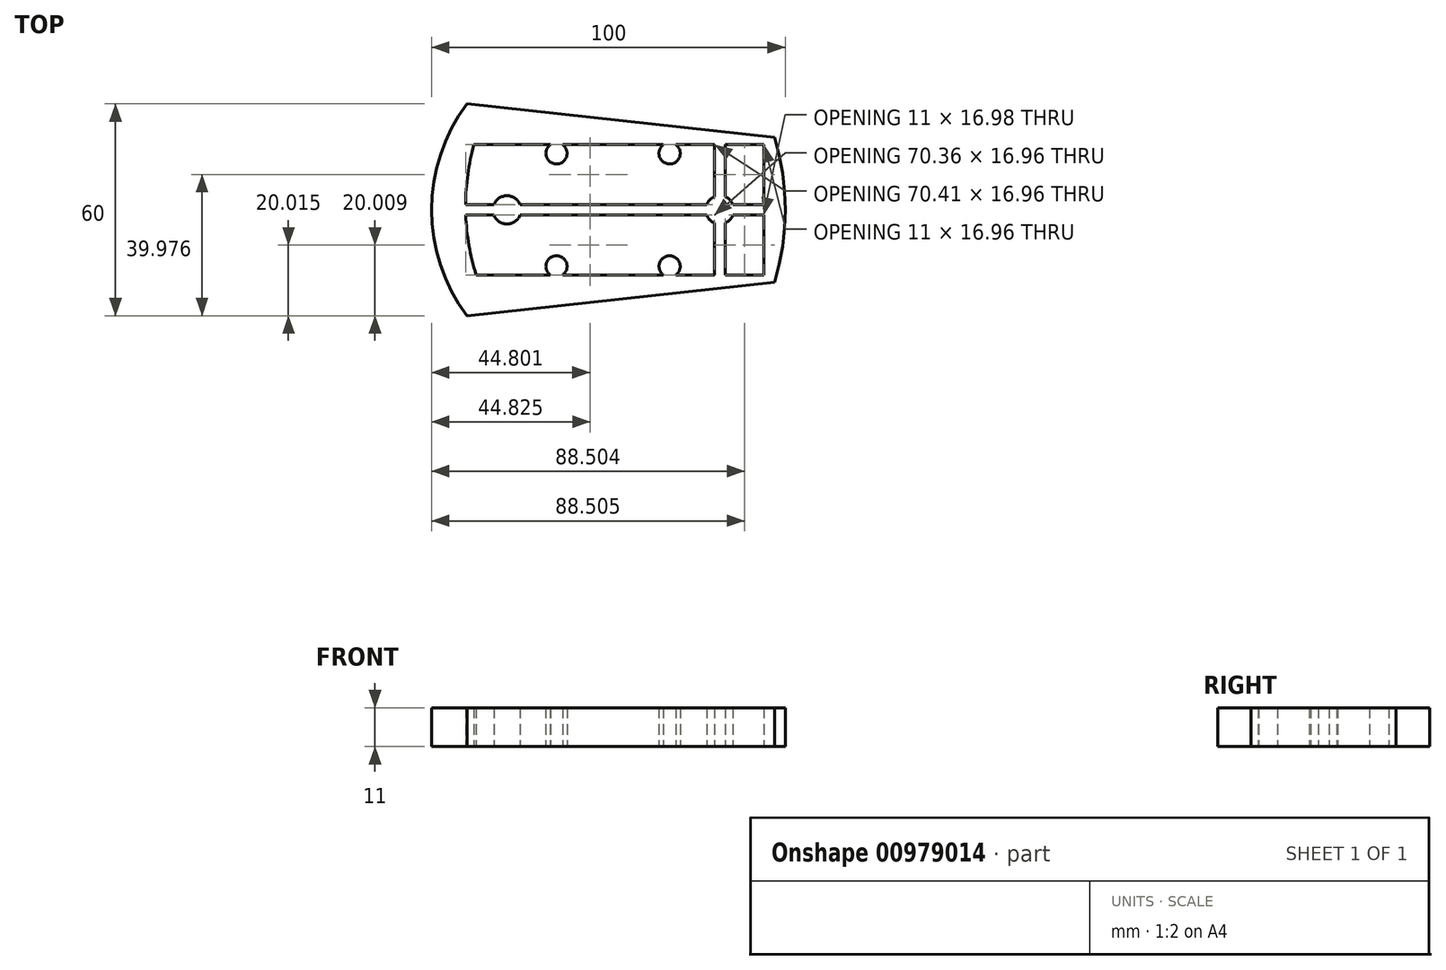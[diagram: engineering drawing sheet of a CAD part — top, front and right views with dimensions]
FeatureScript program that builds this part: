
annotation { "Feature Type Name" : "Feature", "Feature Type Description" : "" }
export const myFeature = defineFeature(function(context is Context, id is Id, definition is map)
    precondition{}
    {
        {
            var Q0;
            Q0=qCreatedBy(makeId("Top.planeOp"),FACE);
            var sketch = newSketch(context, id + "F0", { "sketchPlane" : qUnion([Q0])});
            skLineSegment(sketch, "E0.bottom", {"start": v(-45.83, -20.28) * mm, "end": v(42.17, -20.28) * mm});
            skLineSegment(sketch, "E0.top", {"start": v(-45.83, 20.72) * mm, "end": v(42.17, 20.72) * mm});
            skLineSegment(sketch, "E0.right", {"start": v(42.17, -20.28) * mm, "end": v(42.17, 20.72) * mm});
            skPoint(sketch, "E0.middle", {"position": v(-1.83, 0.22) * mm});
            skLineSegment(sketch, "E1", {"start": v(42.17, 20.72) * mm, "end": v(-44.83, 30.22) * mm});
            skLineSegment(sketch, "E2.MirrorCS", {"start": v(42.17, -20.28) * mm, "end": v(-44.83, -29.78) * mm});
            skArc(sketch, "E3", {"start": v(-44.83, 30.22) * mm, "mid": v(-54.83, 0.22) * mm, "end": v(-44.83, -29.78) * mm});
            skArc(sketch, "E4", {"start": v(42.17, -20.28) * mm, "mid": v(45.17, 0.22) * mm, "end": v(42.17, 20.72) * mm});
            skLineSegment(sketch, "E5.1", {"start": v(-42.25, -18.19) * mm, "end": v(39.17, -18.26) * mm});
            skLineSegment(sketch, "E5.2", {"start": v(39.17, -18.26) * mm, "end": v(39.17, 18.68) * mm});
            skLineSegment(sketch, "E5.3", {"start": v(-42.85, 18.68) * mm, "end": v(39.17, 18.68) * mm});
            skArc(sketch, "E6", {"start": v(-45.83, 20.72) * mm, "mid": v(-48.83, 0.22) * mm, "end": v(-45.83, -20.28) * mm});
            skArc(sketch, "E7", {"start": v(-42.85, 18.68) * mm, "mid": v(-45.23, 0.2) * mm, "end": v(-42.25, -18.19) * mm});
            skPoint(sketch, "E8", {"position": v(26.67, 0.22) * mm});
            skPoint(sketch, "E9", {"position": v(-33.53, 0.22) * mm});
            skPoint(sketch, "E10", {"position": v(-19.53, 16.22) * mm});
            skPoint(sketch, "E11", {"position": v(-19.53, -15.78) * mm});
            skPoint(sketch, "E12", {"position": v(44.47, 16.22) * mm});
            skCircle(sketch, "E13", {"center": v(-19.53, 16.22) * mm, "radius": 3 * mm});
            skCircle(sketch, "E14", {"center": v(-19.53, 16.22) * mm, "radius": 1.3 * mm});
            skCircle(sketch, "E15.MirrorC", {"center": v(12.47, 16.22) * mm, "radius": 1.3 * mm});
            skCircle(sketch, "E16.MirrorC", {"center": v(-19.53, -15.78) * mm, "radius": 3 * mm});
            skCircle(sketch, "E17.MirrorC", {"center": v(12.47, 16.22) * mm, "radius": 3 * mm});
            skCircle(sketch, "E18.MirrorC", {"center": v(-19.53, -15.78) * mm, "radius": 1.3 * mm});
            skPoint(sketch, "E19.MirrorP", {"position": v(12.47, -15.78) * mm});
            skCircle(sketch, "E20.1.0.0", {"center": v(12.47, -15.78) * mm, "radius": 3 * mm});
            skCircle(sketch, "E20.1.0.1", {"center": v(12.47, -15.78) * mm, "radius": 1.3 * mm});
            skLineSegment(sketch, "E20.direction1", {"start": v(-19.53, -15.78) * mm, "end": v(12.47, -15.78) * mm, "construction": true});
            skCircle(sketch, "E21", {"center": v(-33.53, 0.22) * mm, "radius": 4 * mm});
            skCircle(sketch, "E22", {"center": v(-33.53, 0.22) * mm, "radius": 1.3 * mm});
            skCircle(sketch, "E23.1.0.0", {"center": v(26.67, 0.22) * mm, "radius": 1.3 * mm});
            skArc(sketch, "E23.1.0.1", {"start": v(28.17, -3.5) * mm, "mid": v(30.67, 0.22) * mm, "end": v(28.17, 3.93) * mm});
            skLineSegment(sketch, "E23.direction1", {"start": v(-33.53, 0.22) * mm, "end": v(26.67, 0.22) * mm, "construction": true});
            skLineSegment(sketch, "E24", {"start": v(-45.23, 1.72) * mm, "end": v(39.17, 1.72) * mm});
            skLineSegment(sketch, "E25.direction1", {"start": v(-45.23, 1.72) * mm, "end": v(-45.23, 1.72) * mm});
            skLineSegment(sketch, "E26", {"start": v(-45.18, -1.28) * mm, "end": v(39.17, -1.28) * mm});
            skLineSegment(sketch, "E27", {"start": v(11.95, 13.25) * mm, "end": v(11.95, -12.83) * mm});
            skLineSegment(sketch, "E28", {"start": v(14.9, 14.42) * mm, "end": v(14.9, -14) * mm});
            skLineSegment(sketch, "E29", {"start": v(25.17, 3.93) * mm, "end": v(25.17, 18.68) * mm});
            skLineSegment(sketch, "E30", {"start": v(28.17, 3.93) * mm, "end": v(28.17, 18.68) * mm});
            skLineSegment(sketch, "E31", {"start": v(-21.37, -13.42) * mm, "end": v(-21.37, -1.28) * mm});
            skLineSegment(sketch, "E32", {"start": v(-21.37, 1.72) * mm, "end": v(-21.37, 13.85) * mm});
            skLineSegment(sketch, "E33", {"start": v(-4.83, -18.22) * mm, "end": v(-4.83, -1.28) * mm});
            skLineSegment(sketch, "E34", {"start": v(-4.83, -1.28) * mm, "end": v(-4.83, 1.72) * mm});
            skLineSegment(sketch, "E35", {"start": v(-4.83, 1.72) * mm, "end": v(-4.83, 18.68) * mm});
            skArc(sketch, "E36.trimOffspring", {"start": v(25.17, 3.93) * mm, "mid": v(22.67, 0.22) * mm, "end": v(25.17, -3.5) * mm});
            skArc(sketch, "E37", {"start": v(25.17, 3.93) * mm, "mid": v(30.67, 0.22) * mm, "end": v(25.17, -3.5) * mm});
            skLineSegment(sketch, "E38", {"start": v(25.17, -3.5) * mm, "end": v(25.17, -18.25) * mm});
            skLineSegment(sketch, "E39", {"start": v(28.17, -3.5) * mm, "end": v(28.17, -18.25) * mm});
            skSolve(sketch);
        }
        {
            var Q0;
            Q0=makeQuery(id+"F0.imprint","IMPRINT",FACE,{"disambiguationData":[TD([[makeQuery(id+"F0.imprint","IMPRINT",EDGE,{"derivedFrom":sQuery(id+"F0.wireOp",EDGE,"E0.bottom")}),-1.0]])]});
            var Q1;
            {var subQ0=sQuery(id+"F0.wireOp",EDGE,"E38");Q1=makeQuery(id+"F0.imprint","IMPRINT",FACE,{"disambiguationData":[TD([[makeQuery(id+"F0.imprint","IMPRINT",EDGE,{"derivedFrom":subQ0}),1.0]])]});}
            var Q2;
            {var subQ0=sQuery(id+"F0.wireOp",EDGE,"E26");var subQ1=sQuery(id+"F0.wireOp",EDGE,"E21");var subQ2=makeQuery(id+"F0.imprint","INTERSECT",VERTEX,{"disambiguationData":[OD(0.0)],"derivedFrom":[subQ1,subQ0]});Q2=makeQuery(id+"F0.imprint","IMPRINT",FACE,{"disambiguationData":[TD([[makeQuery(id+"F0.imprint","IMPRINT",EDGE,{"disambiguationData":[TD([[subQ2,-1.0]])],"derivedFrom":subQ1}),1.0]])]});}
            var Q3;
            Q3=makeQuery(id+"F0.imprint","IMPRINT",FACE,{"disambiguationData":[TD([[makeQuery(id+"F0.imprint","IMPRINT",EDGE,{"derivedFrom":sQuery(id+"F0.wireOp",EDGE,"E18.MirrorC")}),1.0]])]});
            var Q4;
            Q4=makeQuery(id+"F0.imprint","IMPRINT",FACE,{"disambiguationData":[TD([[makeQuery(id+"F0.imprint","IMPRINT",EDGE,{"derivedFrom":sQuery(id+"F0.wireOp",EDGE,"E0.right")}),-1.0]])]});
            var Q5;
            Q5=makeQuery(id+"F0.imprint","IMPRINT",FACE,{"disambiguationData":[TD([[makeQuery(id+"F0.imprint","IMPRINT",EDGE,{"derivedFrom":sQuery(id+"F0.wireOp",EDGE,"E15.MirrorC")}),-1.0]])]});
            var Q6;
            {var subQ0=sQuery(id+"F0.wireOp",EDGE,"E24");var subQ1=sQuery(id+"F0.wireOp",EDGE,"E21");var subQ2=makeQuery(id+"F0.imprint","INTERSECT",VERTEX,{"disambiguationData":[OD(0.0)],"derivedFrom":[subQ1,subQ0]});Q6=makeQuery(id+"F0.imprint","IMPRINT",FACE,{"disambiguationData":[TD([[makeQuery(id+"F0.imprint","IMPRINT",EDGE,{"disambiguationData":[TD([[subQ2,1.0]])],"derivedFrom":subQ1}),1.0]])]});}
            var Q7;
            Q7=makeQuery(id+"F0.imprint","IMPRINT",FACE,{"disambiguationData":[TD([[makeQuery(id+"F0.imprint","IMPRINT",EDGE,{"derivedFrom":sQuery(id+"F0.wireOp",EDGE,"E20.1.0.1")}),1.0]])]});
            var Q8;
            {var subQ0=sQuery(id+"F0.wireOp",EDGE,"E24");var subQ1=sQuery(id+"F0.wireOp",EDGE,"E5.2");var subQ2=makeQuery(id+"F0.imprint","INTERSECT",VERTEX,{"derivedFrom":[subQ1,subQ0]});Q8=makeQuery(id+"F0.imprint","IMPRINT",FACE,{"disambiguationData":[TD([[makeQuery(id+"F0.imprint","IMPRINT",EDGE,{"disambiguationData":[TD([[subQ2,1.0]])],"derivedFrom":subQ1}),1.0]])]});}
            var Q9;
            Q9=makeQuery(id+"F0.imprint","IMPRINT",FACE,{"disambiguationData":[TD([[makeQuery(id+"F0.imprint","IMPRINT",EDGE,{"derivedFrom":sQuery(id+"F0.wireOp",EDGE,"E15.MirrorC")}),1.0]])]});
            var Q10;
            Q10=makeQuery(id+"F0.imprint","IMPRINT",FACE,{"disambiguationData":[TD([[makeQuery(id+"F0.imprint","IMPRINT",EDGE,{"derivedFrom":sQuery(id+"F0.wireOp",EDGE,"E14")}),-1.0]])]});
            var Q11;
            Q11=makeQuery(id+"F0.imprint","IMPRINT",FACE,{"disambiguationData":[TD([[makeQuery(id+"F0.imprint","IMPRINT",EDGE,{"derivedFrom":sQuery(id+"F0.wireOp",EDGE,"E22")}),-1.0]])]});
            var Q12;
            {var subQ0=sQuery(id+"F0.wireOp",EDGE,"E29");Q12=makeQuery(id+"F0.imprint","IMPRINT",FACE,{"disambiguationData":[TD([[makeQuery(id+"F0.imprint","IMPRINT",EDGE,{"derivedFrom":subQ0}),-1.0]])]});}
            var Q13;
            Q13=makeQuery(id+"F0.imprint","IMPRINT",FACE,{"disambiguationData":[TD([[makeQuery(id+"F0.imprint","IMPRINT",EDGE,{"derivedFrom":sQuery(id+"F0.wireOp",EDGE,"E23.1.0.0")}),-1.0]])]});
            var Q14;
            {var subQ0=sQuery(id+"F0.wireOp",EDGE,"E24");var subQ1=sQuery(id+"F0.wireOp",EDGE,"E7");var subQ2=makeQuery(id+"F0.imprint","INTERSECT",VERTEX,{"derivedFrom":[subQ1,subQ0]});Q14=makeQuery(id+"F0.imprint","IMPRINT",FACE,{"disambiguationData":[TD([[makeQuery(id+"F0.imprint","IMPRINT",EDGE,{"disambiguationData":[TD([[subQ2,-1.0]])],"derivedFrom":subQ1}),1.0]])]});}
            var Q15;
            {var subQ0=sQuery(id+"F0.wireOp",EDGE,"E27");var subQ1=sQuery(id+"F0.wireOp",EDGE,"E17.MirrorC");var subQ2=makeQuery(id+"F0.imprint","INTERSECT",VERTEX,{"derivedFrom":[subQ1,subQ0]});Q15=makeQuery(id+"F0.imprint","IMPRINT",FACE,{"disambiguationData":[TD([[makeQuery(id+"F0.imprint","IMPRINT",EDGE,{"disambiguationData":[TD([[subQ2,1.0]])],"derivedFrom":subQ1}),1.0]])]});}
            var Q16;
            {var subQ0=sQuery(id+"F0.wireOp",EDGE,"E27");var subQ1=sQuery(id+"F0.wireOp",EDGE,"E20.1.0.0");var subQ2=makeQuery(id+"F0.imprint","INTERSECT",VERTEX,{"derivedFrom":[subQ1,subQ0]});Q16=makeQuery(id+"F0.imprint","IMPRINT",FACE,{"disambiguationData":[TD([[makeQuery(id+"F0.imprint","IMPRINT",EDGE,{"disambiguationData":[TD([[subQ2,-1.0]])],"derivedFrom":subQ1}),1.0]])]});}
            var Q17;
            {var subQ0=sQuery(id+"F0.wireOp",EDGE,"E34");Q17=makeQuery(id+"F0.imprint","IMPRINT",FACE,{"disambiguationData":[TD([[makeQuery(id+"F0.imprint","IMPRINT",EDGE,{"derivedFrom":subQ0}),-1.0]])]});}
            var Q18;
            {var subQ0=sQuery(id+"F0.wireOp",EDGE,"E27");var subQ1=sQuery(id+"F0.wireOp",EDGE,"E24");var subQ2=makeQuery(id+"F0.imprint","INTERSECT",VERTEX,{"derivedFrom":[subQ1,subQ0]});Q18=makeQuery(id+"F0.imprint","IMPRINT",FACE,{"disambiguationData":[TD([[makeQuery(id+"F0.imprint","IMPRINT",EDGE,{"disambiguationData":[TD([[subQ2,-1.0]])],"derivedFrom":subQ1}),-1.0]])]});}
            var Q19;
            {var subQ6=sQuery(id+"F0.wireOp",EDGE,"E34");Q19=makeQuery(id+"F0.imprint","IMPRINT",FACE,{"disambiguationData":[TD([[makeQuery(id+"F0.imprint","IMPRINT",EDGE,{"derivedFrom":subQ6}),1.0]])]});}
            var Q20;
            {var subQ0=sQuery(id+"F0.wireOp",EDGE,"E28");var subQ1=sQuery(id+"F0.wireOp",EDGE,"E24");var subQ2=makeQuery(id+"F0.imprint","INTERSECT",VERTEX,{"derivedFrom":[subQ1,subQ0]});Q20=makeQuery(id+"F0.imprint","IMPRINT",FACE,{"disambiguationData":[TD([[makeQuery(id+"F0.imprint","IMPRINT",EDGE,{"disambiguationData":[TD([[subQ2,-1.0]])],"derivedFrom":subQ1}),-1.0]])]});}
            var Q21;
            Q21=makeQuery(id+"F0.imprint","IMPRINT",FACE,{"disambiguationData":[TD([[makeQuery(id+"F0.imprint","IMPRINT",EDGE,{"derivedFrom":sQuery(id+"F0.wireOp",EDGE,"E0.bottom")}),1.0]])]});
            var Q22;
            {var subQ0=sQuery(id+"F0.wireOp",EDGE,"E36.trimOffspring");var subQ1=sQuery(id+"F0.wireOp",EDGE,"E24");var subQ2=makeQuery(id+"F0.imprint","INTERSECT",VERTEX,{"derivedFrom":[subQ1,subQ0]});Q22=makeQuery(id+"F0.imprint","IMPRINT",FACE,{"disambiguationData":[TD([[makeQuery(id+"F0.imprint","IMPRINT",EDGE,{"disambiguationData":[TD([[subQ2,-1.0]])],"derivedFrom":subQ1}),1.0]])]});}
            var Q23;
            {var subQ0=sQuery(id+"F0.wireOp",EDGE,"E36.trimOffspring");var subQ1=sQuery(id+"F0.wireOp",EDGE,"E26");var subQ2=makeQuery(id+"F0.imprint","INTERSECT",VERTEX,{"derivedFrom":[subQ1,subQ0]});Q23=makeQuery(id+"F0.imprint","IMPRINT",FACE,{"disambiguationData":[TD([[makeQuery(id+"F0.imprint","IMPRINT",EDGE,{"disambiguationData":[TD([[subQ2,-1.0]])],"derivedFrom":subQ1}),-1.0]])]});}
            var Q24;
            Q24=makeQuery(id+"F0.imprint","IMPRINT",FACE,{"disambiguationData":[TD([[makeQuery(id+"F0.imprint","IMPRINT",EDGE,{"derivedFrom":sQuery(id+"F0.wireOp",EDGE,"E14")}),1.0]])]});
            var Q25;
            Q25=makeQuery(id+"F0.imprint","IMPRINT",FACE,{"disambiguationData":[TD([[makeQuery(id+"F0.imprint","IMPRINT",EDGE,{"derivedFrom":sQuery(id+"F0.wireOp",EDGE,"E18.MirrorC")}),-1.0]])]});
            var Q26;
            Q26=makeQuery(id+"F0.imprint","IMPRINT",FACE,{"disambiguationData":[TD([[makeQuery(id+"F0.imprint","IMPRINT",EDGE,{"derivedFrom":sQuery(id+"F0.wireOp",EDGE,"E20.1.0.1")}),-1.0]])]});
            var Q27;
            Q27=makeQuery(id+"F0.imprint","IMPRINT",FACE,{"disambiguationData":[TD([[makeQuery(id+"F0.imprint","IMPRINT",EDGE,{"derivedFrom":sQuery(id+"F0.wireOp",EDGE,"E22")}),1.0]])]});
            var Q28;
            Q28=makeQuery(id+"F0.imprint","IMPRINT",FACE,{"disambiguationData":[TD([[makeQuery(id+"F0.imprint","IMPRINT",EDGE,{"derivedFrom":sQuery(id+"F0.wireOp",EDGE,"E23.1.0.0")}),1.0]])]});
            var Q29;
            {var subQ0=sQuery(id+"F0.wireOp",EDGE,"E16.MirrorC");var subQ1=sQuery(id+"F0.wireOp",EDGE,"E5.1");var subQ2=makeQuery(id+"F0.imprint","INTERSECT",VERTEX,{"disambiguationData":[OD(0.0)],"derivedFrom":[subQ1,subQ0]});Q29=makeQuery(id+"F0.imprint","IMPRINT",FACE,{"disambiguationData":[TD([[makeQuery(id+"F0.imprint","IMPRINT",EDGE,{"disambiguationData":[TD([[subQ2,-1.0]])],"derivedFrom":subQ1}),-1.0]])]});}
            var Q30;
            {var subQ0=sQuery(id+"F0.wireOp",EDGE,"E20.1.0.0");var subQ1=sQuery(id+"F0.wireOp",EDGE,"E5.1");var subQ2=makeQuery(id+"F0.imprint","INTERSECT",VERTEX,{"disambiguationData":[OD(0.0)],"derivedFrom":[subQ1,subQ0]});Q30=makeQuery(id+"F0.imprint","IMPRINT",FACE,{"disambiguationData":[TD([[makeQuery(id+"F0.imprint","IMPRINT",EDGE,{"disambiguationData":[TD([[subQ2,-1.0]])],"derivedFrom":subQ1}),-1.0]])]});}
            var Q31;
            {var subQ0=sQuery(id+"F0.wireOp",EDGE,"E13");var subQ1=sQuery(id+"F0.wireOp",EDGE,"E5.3");var subQ2=makeQuery(id+"F0.imprint","INTERSECT",VERTEX,{"disambiguationData":[OD(0.0)],"derivedFrom":[subQ1,subQ0]});Q31=makeQuery(id+"F0.imprint","IMPRINT",FACE,{"disambiguationData":[TD([[makeQuery(id+"F0.imprint","IMPRINT",EDGE,{"disambiguationData":[TD([[subQ2,-1.0]])],"derivedFrom":subQ1}),1.0]])]});}
            var Q32;
            {var subQ0=sQuery(id+"F0.wireOp",EDGE,"E17.MirrorC");var subQ1=sQuery(id+"F0.wireOp",EDGE,"E5.3");var subQ2=makeQuery(id+"F0.imprint","INTERSECT",VERTEX,{"disambiguationData":[OD(0.0)],"derivedFrom":[subQ1,subQ0]});Q32=makeQuery(id+"F0.imprint","IMPRINT",FACE,{"disambiguationData":[TD([[makeQuery(id+"F0.imprint","IMPRINT",EDGE,{"disambiguationData":[TD([[subQ2,-1.0]])],"derivedFrom":subQ1}),1.0]])]});}
            extrude(context, id + "F1", {"entities" : qUnion([Q0, Q1, Q2, Q3, Q4, Q5, Q6, Q7, Q8, Q9, Q10, Q11, Q12, Q13, Q14, Q15, Q16, Q17, Q18, Q19, Q20, Q21, Q22, Q23, Q24, Q25, Q26, Q27, Q28, Q29, Q30, Q31, Q32]), "depth" : 11 * mm, "offsetDistance" : 25 * mm});
        }
    });
